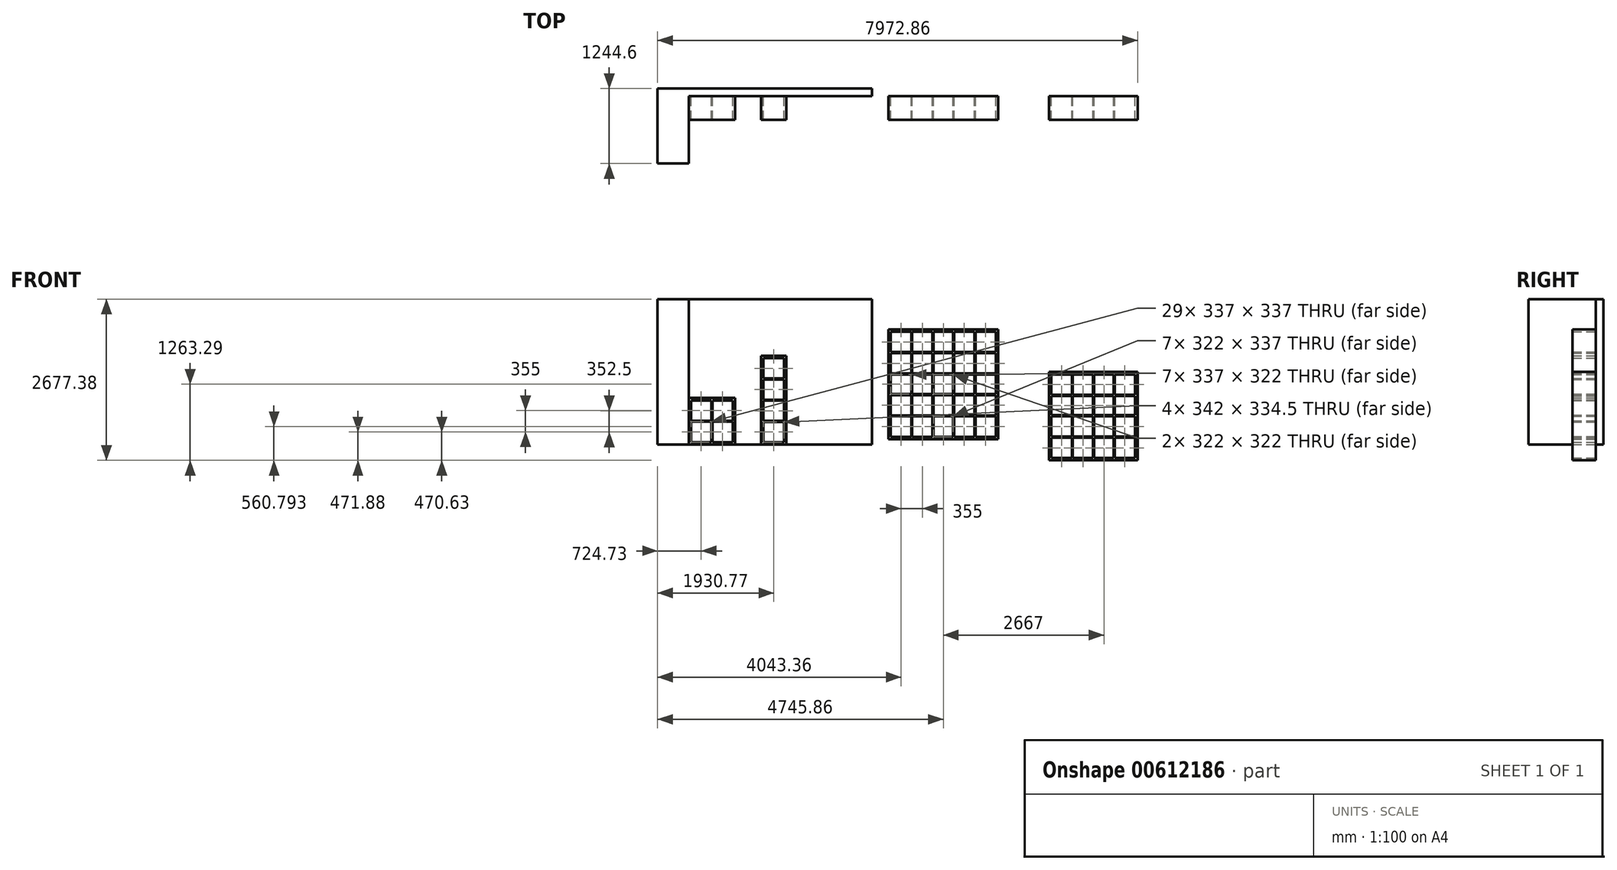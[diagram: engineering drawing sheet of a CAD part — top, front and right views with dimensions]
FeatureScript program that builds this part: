
annotation { "Feature Type Name" : "Feature", "Feature Type Description" : "" }
export const myFeature = defineFeature(function(context is Context, id is Id, definition is map)
    precondition{}
    {
        {
            var Q0;
            Q0=qCreatedBy(makeId("Front.planeOp"),FACE);
            var sketch = newSketch(context, id + "F0", { "sketchPlane" : qUnion([Q0])});
            skLineSegment(sketch, "E0.bottom", {"start": v(0, 0) * mm, "end": v(2806.7, 0) * mm});
            skLineSegment(sketch, "E0.top", {"start": v(0, 2413) * mm, "end": v(2806.7, 2413) * mm});
            skLineSegment(sketch, "E0.left", {"start": v(0, 0) * mm, "end": v(0, 2413) * mm});
            skLineSegment(sketch, "E0.right", {"start": v(2806.7, 0) * mm, "end": v(2806.7, 2413) * mm});
            skSolve(sketch);
        }
        {
            var Q0;
            Q0=qCreatedBy(makeId("Front.planeOp"),FACE);
            var sketch = newSketch(context, id + "F1", { "sketchPlane" : qUnion([Q0])});
            skPoint(sketch, "E1.0", {"position": v(0, 2413) * mm});
            skPoint(sketch, "E2.0", {"position": v(0, 0) * mm});
            skLineSegment(sketch, "E3.0", {"start": v(0, 0) * mm, "end": v(0, 2413) * mm});
            skLineSegment(sketch, "E4", {"start": v(0, 2413) * mm, "end": v(-517.23, 2413) * mm});
            skLineSegment(sketch, "E5", {"start": v(-517.23, 2413) * mm, "end": v(-517.23, 0) * mm});
            skLineSegment(sketch, "E6", {"start": v(-517.23, 0) * mm, "end": v(0, 0) * mm});
            skSolve(sketch);
        }
        {
            var Q0;
            Q0 = qSketchRegion(id + "F1", true);
            extrude(context, id + "F2", {"entities" : qUnion([Q0]), "depth" : 1117.6 * mm, "offsetDistance" : 25 * mm});
        }
        {
            var Q0;
            Q0=makeQuery(id+"F0.imprint","IMPRINT",FACE,{"disambiguationData":[TD([[makeQuery(id+"F0.imprint","IMPRINT",EDGE,{"derivedFrom":sQuery(id+"F0.wireOp",EDGE,"E0.bottom")}),1.0]])]});
            var sketch = newSketch(context, id + "F3", { "sketchPlane" : qUnion([Q0])});
            skPoint(sketch, "E7.0", {"position": v(2806.7, 2413) * mm});
            skPoint(sketch, "E8.0", {"position": v(2806.7, 0) * mm});
            skLineSegment(sketch, "E9", {"start": v(2806.7, 2413) * mm, "end": v(3041, 2413) * mm});
            skLineSegment(sketch, "E10", {"start": v(3041, 2413) * mm, "end": v(3041, 0) * mm});
            skLineSegment(sketch, "E11", {"start": v(3041, 0) * mm, "end": v(2806.7, 0) * mm});
            skLineSegment(sketch, "E12.0", {"start": v(2806.7, 0) * mm, "end": v(2806.7, 2413) * mm});
            skSolve(sketch);
        }
        {
            var Q0;
            Q0=makeQuery(id+"F3.imprint","IMPRINT",FACE,{"disambiguationData":[TD([[makeQuery(id+"F3.imprint","IMPRINT",EDGE,{"derivedFrom":sQuery(id+"F3.wireOp",EDGE,"E12.0")}),1.0]])]});
            var sketch = newSketch(context, id + "F4", { "sketchPlane" : qUnion([Q0])});
            skPoint(sketch, "E13.0", {"position": v(3041, 2413) * mm});
            skLineSegment(sketch, "E14.0", {"start": v(3041, 2413) * mm, "end": v(3041, 0) * mm});
            skLineSegment(sketch, "E15.0", {"start": v(2806.7, 2413) * mm, "end": v(3041, 2413) * mm});
            skLineSegment(sketch, "E16.0", {"start": v(0, 2413) * mm, "end": v(2806.7, 2413) * mm});
            skPoint(sketch, "E17.0", {"position": v(2923.85, 0) * mm});
            skLineSegment(sketch, "E18.0", {"start": v(3041, 0) * mm, "end": v(2806.7, 0) * mm});
            skLineSegment(sketch, "E19.0", {"start": v(0, 0) * mm, "end": v(2806.7, 0) * mm});
            skLineSegment(sketch, "E20.0", {"start": v(-517.23, 0) * mm, "end": v(0, 0) * mm});
            skLineSegment(sketch, "E21.0", {"start": v(-517.23, 2413) * mm, "end": v(-517.23, 0) * mm});
            skLineSegment(sketch, "E22.0", {"start": v(0, 2413) * mm, "end": v(-517.23, 2413) * mm});
            skSolve(sketch);
        }
        {
            var Q0;
            Q0 = qSketchRegion(id + "F4", true);
            extrude(context, id + "F5", {"entities" : qUnion([Q0]), "operationType" : NewBodyOperationType.ADD, "oppositeDirection" : true, "depth" : 127 * mm, "offsetDistance" : 25 * mm});
        }
        {
            var Q0;
            Q0=makeQuery(id+"F0.imprint","IMPRINT",FACE,{"disambiguationData":[TD([[makeQuery(id+"F0.imprint","IMPRINT",EDGE,{"derivedFrom":sQuery(id+"F0.wireOp",EDGE,"E0.bottom")}),1.0]])]});
            var sketch = newSketch(context, id + "F6", { "sketchPlane" : qUnion([Q0])});
            skLineSegment(sketch, "E23.bottom", {"start": v(0, 0) * mm, "end": v(770, 0) * mm});
            skLineSegment(sketch, "E23.top", {"start": v(0, 770) * mm, "end": v(770, 770) * mm});
            skLineSegment(sketch, "E23.left", {"start": v(0, 0) * mm, "end": v(0, 770) * mm});
            skLineSegment(sketch, "E23.right", {"start": v(770, 0) * mm, "end": v(770, 770) * mm});
            skLineSegment(sketch, "E24", {"start": v(39, 731) * mm, "end": v(376, 731) * mm});
            skLineSegment(sketch, "E25", {"start": v(731, 731) * mm, "end": v(731, 394) * mm});
            skLineSegment(sketch, "E26", {"start": v(731, 39) * mm, "end": v(394, 39) * mm});
            skLineSegment(sketch, "E27", {"start": v(39, 39) * mm, "end": v(39, 376) * mm});
            skLineSegment(sketch, "E28", {"start": v(385, 731) * mm, "end": v(385, 39) * mm, "construction": true});
            skLineSegment(sketch, "E29", {"start": v(39, 385) * mm, "end": v(731, 385) * mm, "construction": true});
            skLineSegment(sketch, "E30", {"start": v(376, 731) * mm, "end": v(376, 394) * mm});
            skLineSegment(sketch, "E31", {"start": v(39, 394) * mm, "end": v(376, 394) * mm});
            skLineSegment(sketch, "E32.MirrorCS", {"start": v(39, 376) * mm, "end": v(376, 376) * mm});
            skLineSegment(sketch, "E33.MirrorCS", {"start": v(394, 731) * mm, "end": v(394, 394) * mm});
            skLineSegment(sketch, "E34.trimOffspring", {"start": v(394, 394) * mm, "end": v(731, 394) * mm});
            skLineSegment(sketch, "E35.trimOffspring", {"start": v(376, 376) * mm, "end": v(376, 39) * mm});
            skLineSegment(sketch, "E36.trimOffspring", {"start": v(394, 376) * mm, "end": v(731, 376) * mm});
            skLineSegment(sketch, "E37.trimOffspring", {"start": v(394, 376) * mm, "end": v(394, 39) * mm});
            skLineSegment(sketch, "E38.trimOffspring", {"start": v(39, 394) * mm, "end": v(39, 731) * mm});
            skLineSegment(sketch, "E39.trimOffspring", {"start": v(376, 39) * mm, "end": v(39, 39) * mm});
            skLineSegment(sketch, "E40.trimOffspring", {"start": v(731, 376) * mm, "end": v(731, 39) * mm});
            skLineSegment(sketch, "E41.trimOffspring", {"start": v(394, 731) * mm, "end": v(731, 731) * mm});
            skSolve(sketch);
        }
        {
            var Q0;
            Q0 = qSketchRegion(id + "F6", true);
            extrude(context, id + "F7", {"entities" : qUnion([Q0]), "depth" : 390 * mm, "offsetDistance" : 25 * mm});
        }
        {
            var Q0;
            Q0=makeQuery(id+"F0.imprint","IMPRINT",FACE,{"disambiguationData":[TD([[makeQuery(id+"F0.imprint","IMPRINT",EDGE,{"derivedFrom":sQuery(id+"F0.wireOp",EDGE,"E0.bottom")}),1.0]])]});
            var sketch = newSketch(context, id + "F8", { "sketchPlane" : qUnion([Q0])});
            skLineSegment(sketch, "E42.bottom", {"start": v(1203.54, 0) * mm, "end": v(1623.54, 0) * mm});
            skLineSegment(sketch, "E42.left", {"start": v(1203.54, 0) * mm, "end": v(1203.54, 1470) * mm});
            skLineSegment(sketch, "E43", {"start": v(1242.54, 39) * mm, "end": v(1242.54, 373.5) * mm});
            skLineSegment(sketch, "E44.trimOffspring", {"start": v(1584.54, 39) * mm, "end": v(1242.54, 39) * mm});
            skLineSegment(sketch, "E45", {"start": v(1203.54, 1470) * mm, "end": v(1623.54, 1470) * mm});
            skLineSegment(sketch, "E46", {"start": v(1623.54, 1470) * mm, "end": v(1623.54, 0) * mm});
            skLineSegment(sketch, "E47", {"start": v(1584.54, 39) * mm, "end": v(1584.54, 373.5) * mm});
            skLineSegment(sketch, "E48", {"start": v(1584.54, 1431) * mm, "end": v(1242.54, 1431) * mm});
            skLineSegment(sketch, "E49", {"start": v(1242.54, 735) * mm, "end": v(1584.54, 735) * mm, "construction": true});
            skLineSegment(sketch, "E50", {"start": v(1242.54, 744) * mm, "end": v(1584.54, 744) * mm});
            skLineSegment(sketch, "E51.MirrorCS", {"start": v(1242.54, 726) * mm, "end": v(1584.54, 726) * mm});
            skLineSegment(sketch, "E52.trimOffspring", {"start": v(1242.54, 744) * mm, "end": v(1242.54, 1078.5) * mm});
            skLineSegment(sketch, "E53.trimOffspring", {"start": v(1584.54, 744) * mm, "end": v(1584.54, 1078.5) * mm});
            skLineSegment(sketch, "E54", {"start": v(1242.54, 382.5) * mm, "end": v(1584.54, 382.5) * mm, "construction": true});
            skLineSegment(sketch, "E55", {"start": v(1242.54, 391.5) * mm, "end": v(1584.54, 391.5) * mm});
            skLineSegment(sketch, "E56.MirrorCS", {"start": v(1242.54, 373.5) * mm, "end": v(1584.54, 373.5) * mm});
            skLineSegment(sketch, "E57.trimOffspring", {"start": v(1242.54, 391.5) * mm, "end": v(1242.54, 726) * mm});
            skLineSegment(sketch, "E58.trimOffspring", {"start": v(1584.54, 391.5) * mm, "end": v(1584.54, 726) * mm});
            skLineSegment(sketch, "E59.MirrorCS", {"start": v(1242.54, 1078.5) * mm, "end": v(1584.54, 1078.5) * mm});
            skLineSegment(sketch, "E60.MirrorCS", {"start": v(1242.54, 1096.5) * mm, "end": v(1584.54, 1096.5) * mm});
            skLineSegment(sketch, "E61.MirrorCS", {"start": v(1242.54, 1087.5) * mm, "end": v(1584.54, 1087.5) * mm, "construction": true});
            skLineSegment(sketch, "E62.trimOffspring", {"start": v(1242.54, 1096.5) * mm, "end": v(1242.54, 1431) * mm});
            skLineSegment(sketch, "E63.trimOffspring", {"start": v(1584.54, 1096.5) * mm, "end": v(1584.54, 1431) * mm});
            skSolve(sketch);
        }
        {
            var Q0;
            Q0 = qSketchRegion(id + "F8", true);
            extrude(context, id + "F9", {"entities" : qUnion([Q0]), "depth" : 390 * mm, "offsetDistance" : 25 * mm});
        }
        {
            var Q0;
            Q0=makeQuery(id+"F0.imprint","IMPRINT",FACE,{"disambiguationData":[TD([[makeQuery(id+"F0.imprint","IMPRINT",EDGE,{"derivedFrom":sQuery(id+"F0.wireOp",EDGE,"E0.bottom")}),1.0]])]});
            var sketch = newSketch(context, id + "F10", { "sketchPlane" : qUnion([Q0])});
            skLineSegment(sketch, "E64.bottom", {"start": v(3318.64, 88.91) * mm, "end": v(5138.64, 88.91) * mm});
            skLineSegment(sketch, "E64.left", {"start": v(3318.64, 88.91) * mm, "end": v(3318.64, 1908.91) * mm});
            skLineSegment(sketch, "E65", {"start": v(4049.64, 127.91) * mm, "end": v(3712.64, 127.91) * mm});
            skLineSegment(sketch, "E66", {"start": v(3357.64, 127.91) * mm, "end": v(3357.64, 464.91) * mm});
            skLineSegment(sketch, "E67", {"start": v(3703.64, 819.91) * mm, "end": v(3703.64, 127.91) * mm, "construction": true});
            skLineSegment(sketch, "E68", {"start": v(3357.64, 473.91) * mm, "end": v(4045.3, 473.91) * mm, "construction": true});
            skLineSegment(sketch, "E69", {"start": v(3694.64, 819.91) * mm, "end": v(3694.64, 482.91) * mm});
            skLineSegment(sketch, "E70", {"start": v(3357.64, 482.91) * mm, "end": v(3694.64, 482.91) * mm});
            skLineSegment(sketch, "E71.MirrorCS", {"start": v(3357.64, 464.91) * mm, "end": v(3694.64, 464.91) * mm});
            skLineSegment(sketch, "E72.MirrorCS", {"start": v(3712.64, 819.91) * mm, "end": v(3712.64, 482.91) * mm});
            skLineSegment(sketch, "E73.trimOffspring", {"start": v(3712.64, 482.91) * mm, "end": v(4049.64, 482.91) * mm});
            skLineSegment(sketch, "E74.trimOffspring", {"start": v(3694.64, 464.91) * mm, "end": v(3694.64, 127.91) * mm});
            skLineSegment(sketch, "E75.trimOffspring", {"start": v(3712.64, 464.91) * mm, "end": v(4049.64, 464.91) * mm});
            skLineSegment(sketch, "E76.trimOffspring", {"start": v(3712.64, 464.91) * mm, "end": v(3712.64, 127.91) * mm});
            skLineSegment(sketch, "E77.trimOffspring", {"start": v(3357.64, 482.91) * mm, "end": v(3357.64, 819.91) * mm});
            skLineSegment(sketch, "E78.trimOffspring", {"start": v(3694.64, 127.91) * mm, "end": v(3357.64, 127.91) * mm});
            skLineSegment(sketch, "E79", {"start": v(3357.64, 819.91) * mm, "end": v(3694.64, 819.91) * mm});
            skLineSegment(sketch, "E80", {"start": v(4049.64, 127.91) * mm, "end": v(4049.64, 464.91) * mm});
            skLineSegment(sketch, "E81", {"start": v(3318.64, 1908.91) * mm, "end": v(5138.64, 1908.91) * mm});
            skLineSegment(sketch, "E82", {"start": v(5138.64, 1908.91) * mm, "end": v(5138.64, 88.91) * mm});
            skLineSegment(sketch, "E83.trimOffspring", {"start": v(3712.64, 819.91) * mm, "end": v(4049.64, 819.91) * mm});
            skLineSegment(sketch, "E84.trimOffspring", {"start": v(4049.64, 482.91) * mm, "end": v(4049.64, 819.91) * mm});
            skLineSegment(sketch, "E85.left", {"start": v(3694.64, 837.91) * mm, "end": v(3694.64, 1159.91) * mm});
            skLineSegment(sketch, "E85.right", {"start": v(3712.64, 837.91) * mm, "end": v(3712.64, 1159.91) * mm});
            skLineSegment(sketch, "E86.right", {"start": v(4067.64, 127.91) * mm, "end": v(4067.64, 464.91) * mm});
            skLineSegment(sketch, "E87.bottom", {"start": v(4067.64, 464.91) * mm, "end": v(4389.64, 464.91) * mm});
            skLineSegment(sketch, "E87.top", {"start": v(4067.64, 482.91) * mm, "end": v(4389.64, 482.91) * mm});
            skLineSegment(sketch, "E88.top", {"start": v(3357.64, 837.91) * mm, "end": v(3694.64, 837.91) * mm});
            skLineSegment(sketch, "E89", {"start": v(4067.64, 127.91) * mm, "end": v(4389.64, 127.91) * mm});
            skLineSegment(sketch, "E90.trimOffspring", {"start": v(4067.64, 819.91) * mm, "end": v(4389.64, 819.91) * mm});
            skLineSegment(sketch, "E91.trimOffspring", {"start": v(4049.64, 837.91) * mm, "end": v(4049.64, 1159.91) * mm});
            skLineSegment(sketch, "E92.trimOffspring", {"start": v(4067.64, 837.91) * mm, "end": v(4389.64, 837.91) * mm});
            skLineSegment(sketch, "E93.trimOffspring", {"start": v(3712.64, 837.91) * mm, "end": v(4049.64, 837.91) * mm});
            skLineSegment(sketch, "E94.trimOffspring", {"start": v(4067.64, 482.91) * mm, "end": v(4067.64, 819.91) * mm});
            skLineSegment(sketch, "E95.trimOffspring", {"start": v(4067.64, 837.91) * mm, "end": v(4067.64, 1159.91) * mm});
            skLineSegment(sketch, "E96", {"start": v(3318.64, 998.91) * mm, "end": v(5138.64, 998.91) * mm, "construction": true});
            skLineSegment(sketch, "E97", {"start": v(4228.64, 1908.91) * mm, "end": v(4228.64, 127.91) * mm, "construction": true});
            skLineSegment(sketch, "E98.MirrorCS", {"start": v(4744.64, 819.91) * mm, "end": v(4407.64, 819.91) * mm});
            skLineSegment(sketch, "E99.MirrorCS", {"start": v(4407.64, 127.91) * mm, "end": v(4407.64, 464.91) * mm});
            skLineSegment(sketch, "E100.MirrorCS", {"start": v(5099.64, 482.91) * mm, "end": v(4762.64, 482.91) * mm});
            skLineSegment(sketch, "E101.MirrorCS", {"start": v(4407.64, 482.91) * mm, "end": v(4407.64, 819.91) * mm});
            skLineSegment(sketch, "E102.MirrorCS", {"start": v(4744.64, 464.91) * mm, "end": v(4744.64, 127.91) * mm});
            skLineSegment(sketch, "E103.MirrorCS", {"start": v(5099.64, 819.91) * mm, "end": v(4762.64, 819.91) * mm});
            skLineSegment(sketch, "E104.MirrorCS", {"start": v(4744.64, 819.91) * mm, "end": v(4744.64, 482.91) * mm});
            skLineSegment(sketch, "E105.MirrorCS", {"start": v(4744.64, 482.91) * mm, "end": v(4407.64, 482.91) * mm});
            skLineSegment(sketch, "E106.MirrorCS", {"start": v(5099.64, 482.91) * mm, "end": v(5099.64, 819.91) * mm});
            skLineSegment(sketch, "E107.MirrorCS", {"start": v(4762.64, 819.91) * mm, "end": v(4762.64, 482.91) * mm});
            skLineSegment(sketch, "E108.MirrorCS", {"start": v(4762.64, 127.91) * mm, "end": v(5099.64, 127.91) * mm});
            skLineSegment(sketch, "E109.MirrorCS", {"start": v(4407.64, 127.91) * mm, "end": v(4744.64, 127.91) * mm});
            skLineSegment(sketch, "E110.MirrorCS", {"start": v(4389.64, 482.91) * mm, "end": v(4389.64, 819.91) * mm});
            skLineSegment(sketch, "E111.MirrorCS", {"start": v(5099.64, 464.91) * mm, "end": v(4762.64, 464.91) * mm});
            skLineSegment(sketch, "E112.MirrorCS", {"start": v(4753.64, 819.91) * mm, "end": v(4753.64, 127.91) * mm, "construction": true});
            skLineSegment(sketch, "E113.MirrorCS", {"start": v(5099.64, 473.91) * mm, "end": v(4411.97, 473.91) * mm, "construction": true});
            skLineSegment(sketch, "E114.MirrorCS", {"start": v(4744.64, 464.91) * mm, "end": v(4407.64, 464.91) * mm});
            skLineSegment(sketch, "E115.MirrorCS", {"start": v(4762.64, 464.91) * mm, "end": v(4762.64, 127.91) * mm});
            skLineSegment(sketch, "E116.MirrorCS", {"start": v(4744.64, 837.91) * mm, "end": v(4407.64, 837.91) * mm});
            skLineSegment(sketch, "E117.MirrorCS", {"start": v(5099.64, 127.91) * mm, "end": v(5099.64, 464.91) * mm});
            skLineSegment(sketch, "E118.MirrorCS", {"start": v(4389.64, 127.91) * mm, "end": v(4389.64, 464.91) * mm});
            skLineSegment(sketch, "E119.MirrorCS", {"start": v(5099.64, 837.91) * mm, "end": v(4762.64, 837.91) * mm});
            skLineSegment(sketch, "E120.MirrorCS", {"start": v(4067.64, 1177.91) * mm, "end": v(4389.64, 1177.91) * mm});
            skLineSegment(sketch, "E121.MirrorCS", {"start": v(4067.64, 1159.91) * mm, "end": v(4389.64, 1159.91) * mm});
            skLineSegment(sketch, "E122.MirrorCS", {"start": v(4067.64, 1532.91) * mm, "end": v(4389.64, 1532.91) * mm});
            skLineSegment(sketch, "E123.MirrorCS", {"start": v(4067.64, 1514.91) * mm, "end": v(4389.64, 1514.91) * mm});
            skLineSegment(sketch, "E124.MirrorCS", {"start": v(5099.64, 1177.91) * mm, "end": v(4762.64, 1177.91) * mm});
            skLineSegment(sketch, "E125.MirrorCS", {"start": v(5099.64, 1514.91) * mm, "end": v(4762.64, 1514.91) * mm});
            skLineSegment(sketch, "E126.MirrorCS", {"start": v(4407.64, 1869.91) * mm, "end": v(4407.64, 1532.91) * mm});
            skLineSegment(sketch, "E127.MirrorCS", {"start": v(4049.64, 1869.91) * mm, "end": v(4049.64, 1532.91) * mm});
            skLineSegment(sketch, "E128.MirrorCS", {"start": v(4762.64, 1177.91) * mm, "end": v(4762.64, 1514.91) * mm});
            skLineSegment(sketch, "E129.MirrorCS", {"start": v(4744.64, 1514.91) * mm, "end": v(4407.64, 1514.91) * mm});
            skLineSegment(sketch, "E130.MirrorCS", {"start": v(4744.64, 1177.91) * mm, "end": v(4407.64, 1177.91) * mm});
            skLineSegment(sketch, "E131.MirrorCS", {"start": v(3712.64, 1177.91) * mm, "end": v(3712.64, 1514.91) * mm});
            skLineSegment(sketch, "E132.MirrorCS", {"start": v(3357.64, 1514.91) * mm, "end": v(3694.64, 1514.91) * mm});
            skLineSegment(sketch, "E133.MirrorCS", {"start": v(4762.64, 1532.91) * mm, "end": v(4762.64, 1869.91) * mm});
            skLineSegment(sketch, "E134.MirrorCS", {"start": v(3712.64, 1532.91) * mm, "end": v(3712.64, 1869.91) * mm});
            skLineSegment(sketch, "E135.MirrorCS", {"start": v(3357.64, 1177.91) * mm, "end": v(3694.64, 1177.91) * mm});
            skLineSegment(sketch, "E136.MirrorCS", {"start": v(4049.64, 1514.91) * mm, "end": v(4049.64, 1177.91) * mm});
            skLineSegment(sketch, "E137.MirrorCS", {"start": v(4407.64, 1514.91) * mm, "end": v(4407.64, 1177.91) * mm});
            skLineSegment(sketch, "E138.MirrorCS", {"start": v(3712.64, 1177.91) * mm, "end": v(4049.64, 1177.91) * mm});
            skLineSegment(sketch, "E139.MirrorCS", {"start": v(3712.64, 1514.91) * mm, "end": v(4049.64, 1514.91) * mm});
            skLineSegment(sketch, "E140.MirrorCS", {"start": v(5099.64, 1869.91) * mm, "end": v(5099.64, 1532.91) * mm});
            skLineSegment(sketch, "E141.MirrorCS", {"start": v(4744.64, 1177.91) * mm, "end": v(4744.64, 1514.91) * mm});
            skLineSegment(sketch, "E142.MirrorCS", {"start": v(4744.64, 1159.91) * mm, "end": v(4407.64, 1159.91) * mm});
            skLineSegment(sketch, "E143.MirrorCS", {"start": v(4067.64, 1514.91) * mm, "end": v(4067.64, 1177.91) * mm});
            skLineSegment(sketch, "E144.MirrorCS", {"start": v(4762.64, 1869.91) * mm, "end": v(5099.64, 1869.91) * mm});
            skLineSegment(sketch, "E145.MirrorCS", {"start": v(3703.64, 1177.91) * mm, "end": v(3703.64, 1869.91) * mm, "construction": true});
            skLineSegment(sketch, "E146.MirrorCS", {"start": v(3357.64, 1869.91) * mm, "end": v(3357.64, 1532.91) * mm});
            skLineSegment(sketch, "E147.MirrorCS", {"start": v(5099.64, 1514.91) * mm, "end": v(5099.64, 1177.91) * mm});
            skLineSegment(sketch, "E148.MirrorCS", {"start": v(4049.64, 1869.91) * mm, "end": v(3712.64, 1869.91) * mm});
            skLineSegment(sketch, "E149.MirrorCS", {"start": v(4389.64, 1869.91) * mm, "end": v(4389.64, 1532.91) * mm});
            skLineSegment(sketch, "E150.MirrorCS", {"start": v(5099.64, 1523.91) * mm, "end": v(4411.97, 1523.91) * mm, "construction": true});
            skLineSegment(sketch, "E151.MirrorCS", {"start": v(3712.64, 1532.91) * mm, "end": v(4049.64, 1532.91) * mm});
            skLineSegment(sketch, "E152.MirrorCS", {"start": v(3694.64, 1177.91) * mm, "end": v(3694.64, 1514.91) * mm});
            skLineSegment(sketch, "E153.MirrorCS", {"start": v(4753.64, 1177.91) * mm, "end": v(4753.64, 1869.91) * mm, "construction": true});
            skLineSegment(sketch, "E154.MirrorCS", {"start": v(3357.64, 1523.91) * mm, "end": v(4045.3, 1523.91) * mm, "construction": true});
            skLineSegment(sketch, "E155.MirrorCS", {"start": v(5099.64, 1532.91) * mm, "end": v(4762.64, 1532.91) * mm});
            skLineSegment(sketch, "E156.MirrorCS", {"start": v(3357.64, 1532.91) * mm, "end": v(3694.64, 1532.91) * mm});
            skLineSegment(sketch, "E157.MirrorCS", {"start": v(4744.64, 1532.91) * mm, "end": v(4744.64, 1869.91) * mm});
            skLineSegment(sketch, "E158.MirrorCS", {"start": v(4407.64, 1869.91) * mm, "end": v(4744.64, 1869.91) * mm});
            skLineSegment(sketch, "E159.MirrorCS", {"start": v(4067.64, 1869.91) * mm, "end": v(4067.64, 1532.91) * mm});
            skLineSegment(sketch, "E160.MirrorCS", {"start": v(3694.64, 1532.91) * mm, "end": v(3694.64, 1869.91) * mm});
            skLineSegment(sketch, "E161.MirrorCS", {"start": v(3694.64, 1869.91) * mm, "end": v(3357.64, 1869.91) * mm});
            skLineSegment(sketch, "E162.MirrorCS", {"start": v(3712.64, 1159.91) * mm, "end": v(4049.64, 1159.91) * mm});
            skLineSegment(sketch, "E163.MirrorCS", {"start": v(4744.64, 1532.91) * mm, "end": v(4407.64, 1532.91) * mm});
            skLineSegment(sketch, "E164.MirrorCS", {"start": v(5099.64, 1159.91) * mm, "end": v(4762.64, 1159.91) * mm});
            skLineSegment(sketch, "E165.MirrorCS", {"start": v(4389.64, 1514.91) * mm, "end": v(4389.64, 1177.91) * mm});
            skLineSegment(sketch, "E166.MirrorCS", {"start": v(3357.64, 1159.91) * mm, "end": v(3694.64, 1159.91) * mm});
            skLineSegment(sketch, "E167.MirrorCS", {"start": v(3357.64, 1514.91) * mm, "end": v(3357.64, 1177.91) * mm});
            skLineSegment(sketch, "E168", {"start": v(4067.64, 1869.91) * mm, "end": v(4389.64, 1869.91) * mm});
            skLineSegment(sketch, "E169", {"start": v(3357.64, 1159.91) * mm, "end": v(3357.64, 837.91) * mm});
            skLineSegment(sketch, "E170", {"start": v(4389.64, 1159.91) * mm, "end": v(4389.64, 837.91) * mm});
            skLineSegment(sketch, "E171", {"start": v(4407.64, 837.91) * mm, "end": v(4407.64, 1159.91) * mm});
            skLineSegment(sketch, "E172", {"start": v(4744.64, 1159.91) * mm, "end": v(4744.64, 837.91) * mm});
            skLineSegment(sketch, "E173", {"start": v(4762.64, 837.91) * mm, "end": v(4762.64, 1159.91) * mm});
            skLineSegment(sketch, "E174", {"start": v(5099.64, 1159.91) * mm, "end": v(5099.64, 837.91) * mm});
            skPoint(sketch, "E175.orphan", {"position": v(5290, 1159.91) * mm});
            skPoint(sketch, "E176.orphan", {"position": v(5290, 1177.91) * mm});
            skPoint(sketch, "E88.right.end.orphan", {"position": v(5290, 837.91) * mm});
            skPoint(sketch, "E88.right.start.orphan", {"position": v(5290, 819.91) * mm});
            skLineSegment(sketch, "E177.trimOffspring", {"start": v(4762.64, 819.91) * mm, "end": v(5099.64, 819.91) * mm});
            skLineSegment(sketch, "E178.trimOffspring", {"start": v(4762.64, 837.91) * mm, "end": v(5099.64, 837.91) * mm});
            skLineSegment(sketch, "E179.trimOffspring", {"start": v(4762.64, 482.91) * mm, "end": v(5099.64, 482.91) * mm});
            skPoint(sketch, "E87.right.end.orphan", {"position": v(5290, 482.91) * mm});
            skPoint(sketch, "E87.right.start.orphan", {"position": v(5290, 464.91) * mm});
            skLineSegment(sketch, "E180.trimOffspring", {"start": v(4407.64, 837.91) * mm, "end": v(4744.64, 837.91) * mm});
            skLineSegment(sketch, "E181.trimOffspring", {"start": v(4049.64, 1177.91) * mm, "end": v(4049.64, 1514.91) * mm});
            skLineSegment(sketch, "E182.trimOffspring", {"start": v(4067.64, 1177.91) * mm, "end": v(4067.64, 1514.91) * mm});
            skLineSegment(sketch, "E183.trimOffspring", {"start": v(4407.64, 1159.91) * mm, "end": v(4744.64, 1159.91) * mm});
            skLineSegment(sketch, "E184.trimOffspring", {"start": v(4762.64, 1177.91) * mm, "end": v(5099.64, 1177.91) * mm});
            skLineSegment(sketch, "E185.trimOffspring", {"start": v(4762.64, 1159.91) * mm, "end": v(5099.64, 1159.91) * mm});
            skLineSegment(sketch, "E186.trimOffspring", {"start": v(4762.64, 1532.91) * mm, "end": v(5099.64, 1532.91) * mm});
            skPoint(sketch, "E187.trimOffspring.end.orphan", {"position": v(5290, 1532.91) * mm});
            skPoint(sketch, "E188.trimOffspring.end.orphan", {"position": v(5290, 1514.91) * mm});
            skLineSegment(sketch, "E189.trimOffspring", {"start": v(4407.64, 1532.91) * mm, "end": v(4744.64, 1532.91) * mm});
            skLineSegment(sketch, "E190.trimOffspring", {"start": v(4049.64, 1532.91) * mm, "end": v(4049.64, 1869.91) * mm});
            skLineSegment(sketch, "E191.trimOffspring", {"start": v(4067.64, 1532.91) * mm, "end": v(4067.64, 1869.91) * mm});
            skPoint(sketch, "E192.trimOffspring.end.orphan", {"position": v(3712.64, 2166.32) * mm});
            skSolve(sketch);
        }
        {
            var Q0;
            Q0 = qSketchRegion(id + "F10", true);
            extrude(context, id + "F11", {"entities" : qUnion([Q0]), "depth" : 390 * mm, "offsetDistance" : 25 * mm});
        }
        {
            var Q0;
            Q0=makeQuery(id+"F0.imprint","IMPRINT",FACE,{"disambiguationData":[TD([[makeQuery(id+"F0.imprint","IMPRINT",EDGE,{"derivedFrom":sQuery(id+"F0.wireOp",EDGE,"E0.bottom")}),1.0]])]});
            var sketch = newSketch(context, id + "F12", { "sketchPlane" : qUnion([Q0])});
            skLineSegment(sketch, "E193", {"start": v(6716.63, -225.38) * mm, "end": v(6379.63, -225.38) * mm});
            skLineSegment(sketch, "E194", {"start": v(6024.63, -225.38) * mm, "end": v(6024.63, 111.62) * mm});
            skLineSegment(sketch, "E195", {"start": v(6370.63, 466.62) * mm, "end": v(6370.63, -225.38) * mm, "construction": true});
            skLineSegment(sketch, "E196", {"start": v(6024.63, 120.62) * mm, "end": v(6712.3, 120.62) * mm, "construction": true});
            skLineSegment(sketch, "E197", {"start": v(6361.63, 466.62) * mm, "end": v(6361.63, 129.62) * mm});
            skLineSegment(sketch, "E198", {"start": v(6024.63, 129.62) * mm, "end": v(6361.63, 129.62) * mm});
            skLineSegment(sketch, "E199.MirrorCS", {"start": v(6024.63, 111.62) * mm, "end": v(6361.63, 111.62) * mm});
            skLineSegment(sketch, "E200.MirrorCS", {"start": v(6379.63, 466.62) * mm, "end": v(6379.63, 129.62) * mm});
            skLineSegment(sketch, "E201.trimOffspring", {"start": v(6379.63, 129.62) * mm, "end": v(6716.63, 129.62) * mm});
            skLineSegment(sketch, "E202.trimOffspring", {"start": v(6361.63, 111.62) * mm, "end": v(6361.63, -225.38) * mm});
            skLineSegment(sketch, "E203.trimOffspring", {"start": v(6379.63, 111.62) * mm, "end": v(6716.63, 111.62) * mm});
            skLineSegment(sketch, "E204.trimOffspring", {"start": v(6379.63, 111.62) * mm, "end": v(6379.63, -225.38) * mm});
            skLineSegment(sketch, "E205.trimOffspring", {"start": v(6024.63, 129.62) * mm, "end": v(6024.63, 466.62) * mm});
            skLineSegment(sketch, "E206.trimOffspring", {"start": v(6361.63, -225.38) * mm, "end": v(6024.63, -225.38) * mm});
            skLineSegment(sketch, "E207", {"start": v(6024.63, 466.62) * mm, "end": v(6361.63, 466.62) * mm});
            skLineSegment(sketch, "E208", {"start": v(6716.63, -225.38) * mm, "end": v(6716.63, 111.62) * mm});
            skLineSegment(sketch, "E209.trimOffspring", {"start": v(6379.63, 466.62) * mm, "end": v(6716.63, 466.62) * mm});
            skLineSegment(sketch, "E210.trimOffspring", {"start": v(6716.63, 129.62) * mm, "end": v(6716.63, 466.62) * mm});
            skLineSegment(sketch, "E211.left", {"start": v(6361.63, 484.62) * mm, "end": v(6361.63, 806.62) * mm});
            skLineSegment(sketch, "E211.right", {"start": v(6379.63, 484.62) * mm, "end": v(6379.63, 806.62) * mm});
            skLineSegment(sketch, "E212.right", {"start": v(6734.63, -225.38) * mm, "end": v(6734.63, 111.62) * mm});
            skLineSegment(sketch, "E213.bottom", {"start": v(6734.63, 111.62) * mm, "end": v(7056.63, 111.62) * mm});
            skLineSegment(sketch, "E213.top", {"start": v(6734.63, 129.62) * mm, "end": v(7056.63, 129.62) * mm});
            skLineSegment(sketch, "E214.top", {"start": v(6024.63, 484.62) * mm, "end": v(6361.63, 484.62) * mm});
            skLineSegment(sketch, "E215", {"start": v(6734.63, -225.38) * mm, "end": v(7056.63, -225.38) * mm});
            skLineSegment(sketch, "E216.trimOffspring", {"start": v(6734.63, 466.62) * mm, "end": v(7056.63, 466.62) * mm});
            skLineSegment(sketch, "E217.trimOffspring", {"start": v(6716.63, 484.62) * mm, "end": v(6716.63, 806.62) * mm});
            skLineSegment(sketch, "E218.trimOffspring", {"start": v(6734.63, 484.62) * mm, "end": v(7056.63, 484.62) * mm});
            skLineSegment(sketch, "E219.trimOffspring", {"start": v(6379.63, 484.62) * mm, "end": v(6716.63, 484.62) * mm});
            skLineSegment(sketch, "E220.trimOffspring", {"start": v(6734.63, 129.62) * mm, "end": v(6734.63, 466.62) * mm});
            skLineSegment(sketch, "E221.trimOffspring", {"start": v(6734.63, 484.62) * mm, "end": v(6734.63, 806.62) * mm});
            skLineSegment(sketch, "E222", {"start": v(5985.63, 645.62) * mm, "end": v(7411.63, 645.62) * mm, "construction": true});
            skLineSegment(sketch, "E223", {"start": v(6895.63, 1555.62) * mm, "end": v(6895.63, -225.38) * mm, "construction": true});
            skLineSegment(sketch, "E224.MirrorCS", {"start": v(7411.63, 466.62) * mm, "end": v(7074.63, 466.62) * mm});
            skLineSegment(sketch, "E225.MirrorCS", {"start": v(7074.63, -225.38) * mm, "end": v(7074.63, 111.62) * mm});
            skLineSegment(sketch, "E226.MirrorCS", {"start": v(7074.63, 129.62) * mm, "end": v(7074.63, 466.62) * mm});
            skLineSegment(sketch, "E227.MirrorCS", {"start": v(7411.63, 111.62) * mm, "end": v(7411.63, -225.38) * mm});
            skLineSegment(sketch, "E228.MirrorCS", {"start": v(7411.63, 466.62) * mm, "end": v(7411.63, 129.62) * mm});
            skLineSegment(sketch, "E229.MirrorCS", {"start": v(7411.63, 129.62) * mm, "end": v(7074.63, 129.62) * mm});
            skLineSegment(sketch, "E230.MirrorCS", {"start": v(7074.63, -225.38) * mm, "end": v(7411.63, -225.38) * mm});
            skLineSegment(sketch, "E231.MirrorCS", {"start": v(7056.63, 129.62) * mm, "end": v(7056.63, 466.62) * mm});
            skLineSegment(sketch, "E232.MirrorCS", {"start": v(7455.63, 120.62) * mm, "end": v(7078.96, 120.62) * mm, "construction": true});
            skLineSegment(sketch, "E233.MirrorCS", {"start": v(7411.63, 111.62) * mm, "end": v(7074.63, 111.62) * mm});
            skLineSegment(sketch, "E234.MirrorCS", {"start": v(7411.63, 484.62) * mm, "end": v(7074.63, 484.62) * mm});
            skLineSegment(sketch, "E235.MirrorCS", {"start": v(7056.63, -225.38) * mm, "end": v(7056.63, 111.62) * mm});
            skLineSegment(sketch, "E236.MirrorCS", {"start": v(6734.63, 824.62) * mm, "end": v(7056.63, 824.62) * mm});
            skLineSegment(sketch, "E237.MirrorCS", {"start": v(6734.63, 806.62) * mm, "end": v(7056.63, 806.62) * mm});
            skLineSegment(sketch, "E238.MirrorCS", {"start": v(6734.63, 1161.62) * mm, "end": v(7056.63, 1161.62) * mm});
            skLineSegment(sketch, "E239.MirrorCS", {"start": v(7411.63, 1161.62) * mm, "end": v(7074.63, 1161.62) * mm});
            skLineSegment(sketch, "E240.MirrorCS", {"start": v(7411.63, 824.62) * mm, "end": v(7074.63, 824.62) * mm});
            skLineSegment(sketch, "E241.MirrorCS", {"start": v(6379.63, 824.62) * mm, "end": v(6379.63, 1161.62) * mm});
            skLineSegment(sketch, "E242.MirrorCS", {"start": v(6024.63, 1161.62) * mm, "end": v(6361.63, 1161.62) * mm});
            skLineSegment(sketch, "E243.MirrorCS", {"start": v(6024.63, 824.62) * mm, "end": v(6361.63, 824.62) * mm});
            skLineSegment(sketch, "E244.MirrorCS", {"start": v(6716.63, 1161.62) * mm, "end": v(6716.63, 824.62) * mm});
            skLineSegment(sketch, "E245.MirrorCS", {"start": v(7074.63, 1161.62) * mm, "end": v(7074.63, 824.62) * mm});
            skLineSegment(sketch, "E246.MirrorCS", {"start": v(6379.63, 824.62) * mm, "end": v(6716.63, 824.62) * mm});
            skLineSegment(sketch, "E247.MirrorCS", {"start": v(6379.63, 1161.62) * mm, "end": v(6716.63, 1161.62) * mm});
            skLineSegment(sketch, "E248.MirrorCS", {"start": v(7411.63, 824.62) * mm, "end": v(7411.63, 1161.62) * mm});
            skLineSegment(sketch, "E249.MirrorCS", {"start": v(7411.63, 806.62) * mm, "end": v(7074.63, 806.62) * mm});
            skLineSegment(sketch, "E250.MirrorCS", {"start": v(6734.63, 1161.62) * mm, "end": v(6734.63, 824.62) * mm});
            skLineSegment(sketch, "E251.MirrorCS", {"start": v(6370.63, 824.62) * mm, "end": v(6370.63, 1516.62) * mm, "construction": true});
            skLineSegment(sketch, "E252.MirrorCS", {"start": v(6361.63, 824.62) * mm, "end": v(6361.63, 1161.62) * mm});
            skLineSegment(sketch, "E253.MirrorCS", {"start": v(6379.63, 806.62) * mm, "end": v(6716.63, 806.62) * mm});
            skLineSegment(sketch, "E254.MirrorCS", {"start": v(7056.63, 1161.62) * mm, "end": v(7056.63, 824.62) * mm});
            skLineSegment(sketch, "E255.MirrorCS", {"start": v(6024.63, 806.62) * mm, "end": v(6361.63, 806.62) * mm});
            skLineSegment(sketch, "E256.MirrorCS", {"start": v(6024.63, 1161.62) * mm, "end": v(6024.63, 824.62) * mm});
            skLineSegment(sketch, "E257", {"start": v(6024.63, 806.62) * mm, "end": v(6024.63, 484.62) * mm});
            skLineSegment(sketch, "E258", {"start": v(7056.63, 806.62) * mm, "end": v(7056.63, 484.62) * mm});
            skLineSegment(sketch, "E259", {"start": v(7074.63, 484.62) * mm, "end": v(7074.63, 806.62) * mm});
            skLineSegment(sketch, "E260", {"start": v(7411.63, 806.62) * mm, "end": v(7411.63, 484.62) * mm});
            skLineSegment(sketch, "E261.trimOffspring", {"start": v(7074.63, 484.62) * mm, "end": v(7411.63, 484.62) * mm});
            skLineSegment(sketch, "E262.trimOffspring", {"start": v(6716.63, 824.62) * mm, "end": v(6716.63, 1161.62) * mm});
            skLineSegment(sketch, "E263.trimOffspring", {"start": v(6734.63, 824.62) * mm, "end": v(6734.63, 1161.62) * mm});
            skLineSegment(sketch, "E264.trimOffspring", {"start": v(7074.63, 806.62) * mm, "end": v(7411.63, 806.62) * mm});
            skPoint(sketch, "E265.trimOffspring.end.orphan", {"position": v(6379.63, 1813.02) * mm});
            skLineSegment(sketch, "E266", {"start": v(5985.63, -264.38) * mm, "end": v(5985.63, 1205.62) * mm});
            skLineSegment(sketch, "E267", {"start": v(5985.63, 1205.62) * mm, "end": v(7455.63, 1205.62) * mm});
            skLineSegment(sketch, "E268", {"start": v(5985.63, -264.38) * mm, "end": v(7455.63, -264.38) * mm});
            skLineSegment(sketch, "E269", {"start": v(7455.63, -264.38) * mm, "end": v(7455.63, 1205.62) * mm});
            skPoint(sketch, "E270.orphan", {"position": v(7766.63, 120.62) * mm});
            skSolve(sketch);
        }
        {
            var Q0;
            Q0 = qSketchRegion(id + "F12", true);
            extrude(context, id + "F13", {"entities" : qUnion([Q0]), "depth" : 390 * mm, "offsetDistance" : 25 * mm});
        }
    });
